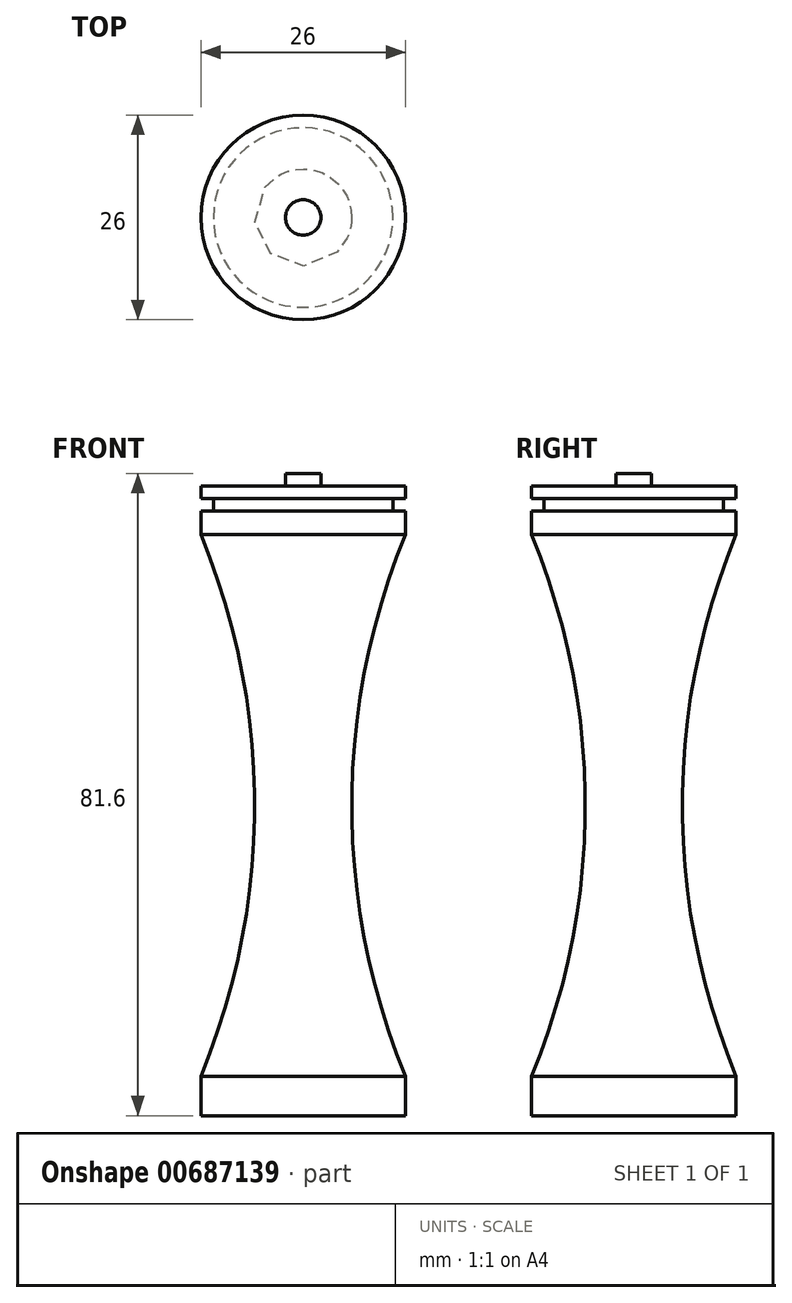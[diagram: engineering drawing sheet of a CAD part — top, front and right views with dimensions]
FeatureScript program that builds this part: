
annotation { "Feature Type Name" : "Feature", "Feature Type Description" : "" }
export const myFeature = defineFeature(function(context is Context, id is Id, definition is map)
    precondition{}
    {
        {
            var Q0;
            Q0=qCreatedBy(makeId("Front.planeOp"),FACE);
            var sketch = newSketch(context, id + "F0", { "sketchPlane" : qUnion([Q0])});
            skLineSegment(sketch, "E0", {"start": v(-13, 49.23) * mm, "end": v(-13, 47.63) * mm});
            skLineSegment(sketch, "E1", {"start": v(-13, 47.63) * mm, "end": v(-11.4, 47.63) * mm});
            skLineSegment(sketch, "E2", {"start": v(-11.4, 47.63) * mm, "end": v(-11.4, 46.03) * mm});
            skLineSegment(sketch, "E3", {"start": v(-11.4, 46.03) * mm, "end": v(-13, 46.03) * mm});
            skLineSegment(sketch, "E4", {"start": v(-13, 46.03) * mm, "end": v(-13, 43.03) * mm});
            skLineSegment(sketch, "E5", {"start": v(-13, -25.77) * mm, "end": v(-13, -30.77) * mm});
            skLineSegment(sketch, "E6", {"start": v(-13, -30.77) * mm, "end": v(0, -30.77) * mm});
            skArc(sketch, "E7", {"start": v(-13, -25.77) * mm, "mid": v(-6.17, 8.63) * mm, "end": v(-13, 43.03) * mm});
            skLineSegment(sketch, "E8", {"start": v(0, 50.83) * mm, "end": v(-2.25, 50.83) * mm});
            skLineSegment(sketch, "E9", {"start": v(-2.25, 50.83) * mm, "end": v(-2.25, 49.23) * mm});
            skLineSegment(sketch, "E10", {"start": v(-2.25, 49.23) * mm, "end": v(-13, 49.23) * mm});
            skLineSegment(sketch, "E11", {"start": v(0, 74.54) * mm, "end": v(0, -75.84) * mm, "construction": true});
            skLineSegment(sketch, "E12", {"start": v(0, 50.83) * mm, "end": v(0, -30.77) * mm});
            skSolve(sketch);
        }
        {
            var Q0;
            Q0 = qSketchRegion(id + "F0", true);
            var Q1;
            Q1=sQuery(id+"F0.wireOp",EDGE,"E12");
            revolve(context, id + "F1", {"entities" : qUnion([Q0]), "axis" : qUnion([Q1]), "revolveType" : RevolveType.FULL});
        }
    });
